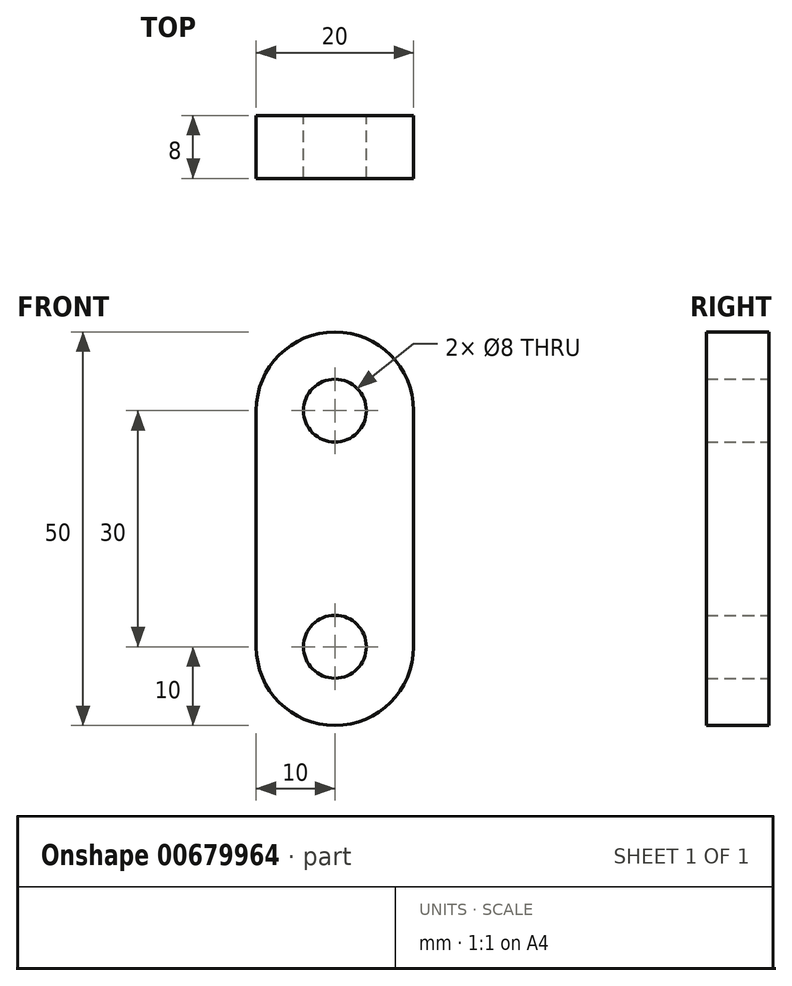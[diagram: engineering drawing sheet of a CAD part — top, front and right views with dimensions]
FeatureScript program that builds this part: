
annotation { "Feature Type Name" : "Feature", "Feature Type Description" : "" }
export const myFeature = defineFeature(function(context is Context, id is Id, definition is map)
    precondition{}
    {
        {
            var Q0;
            Q0=qCreatedBy(makeId("Front.planeOp"),FACE);
            var sketch = newSketch(context, id + "F0", { "sketchPlane" : qUnion([Q0])});
            skArc(sketch, "E0", {"start": v(10, 30) * mm, "mid": v(0, 40) * mm, "end": v(-10, 30) * mm});
            skCircle(sketch, "E1", {"center": v(0, 30) * mm, "radius": 4 * mm});
            skArc(sketch, "E2", {"start": v(-10, 0) * mm, "mid": v(0, -10) * mm, "end": v(10, 0) * mm});
            skCircle(sketch, "E3", {"center": v(0, 0) * mm, "radius": 4 * mm});
            skLineSegment(sketch, "E4", {"start": v(10, 30) * mm, "end": v(10, 0) * mm});
            skLineSegment(sketch, "E5", {"start": v(-10, 30) * mm, "end": v(-10, 0) * mm});
            skSolve(sketch);
        }
        {
            var Q0;
            Q0 = qSketchRegion(id + "F0", true);
            extrude(context, id + "F1", {"entities" : qUnion([Q0]), "depth" : 8 * mm, "offsetDistance" : 25.4 * mm});
        }
    });
